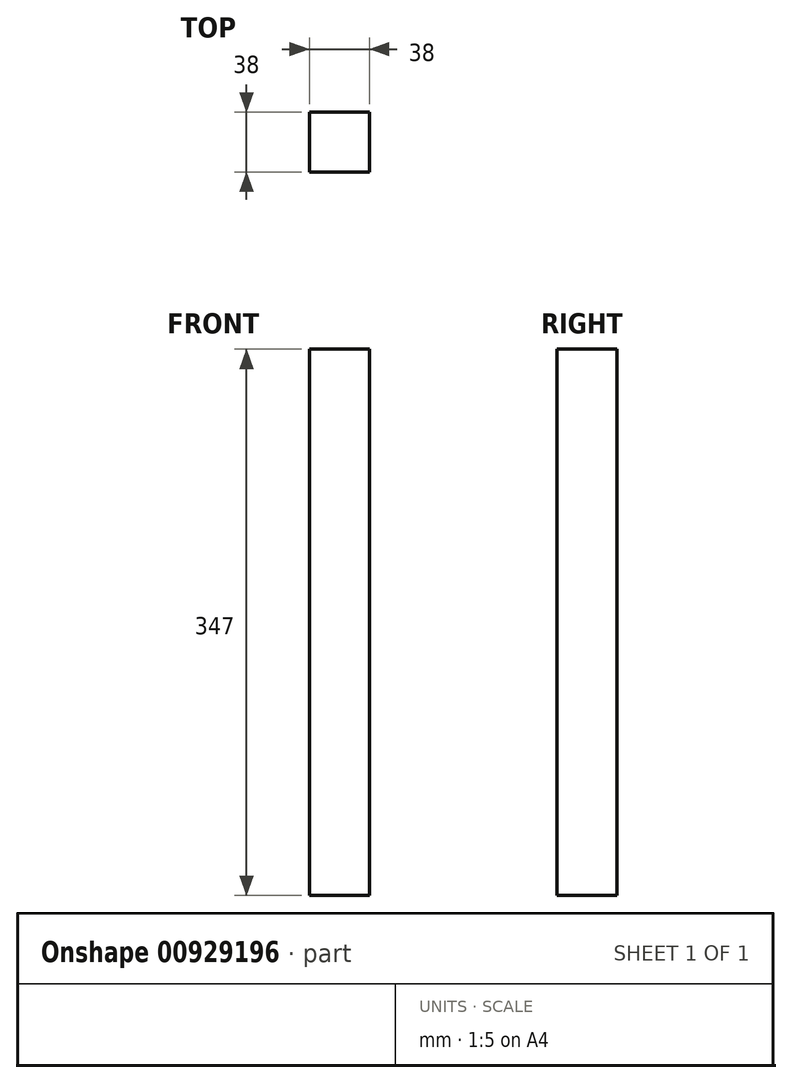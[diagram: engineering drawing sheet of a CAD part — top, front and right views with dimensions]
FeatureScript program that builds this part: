
annotation { "Feature Type Name" : "Feature", "Feature Type Description" : "" }
export const myFeature = defineFeature(function(context is Context, id is Id, definition is map)
    precondition{}
    {
        {
            var Q0;
            Q0=qCreatedBy(makeId("Front.planeOp"),FACE);
            var sketch = newSketch(context, id + "F0", { "sketchPlane" : qUnion([Q0])});
            skLineSegment(sketch, "E0.bottom", {"start": v(-24.87, 284.07) * mm, "end": v(13.13, 284.07) * mm});
            skLineSegment(sketch, "E0.top", {"start": v(-24.87, -62.93) * mm, "end": v(13.13, -62.93) * mm});
            skLineSegment(sketch, "E0.left", {"start": v(-24.87, 284.07) * mm, "end": v(-24.87, -62.93) * mm});
            skLineSegment(sketch, "E0.right", {"start": v(13.13, 284.07) * mm, "end": v(13.13, -62.93) * mm});
            skSolve(sketch);
        }
        {
            var Q0;
            Q0 = qSketchRegion(id + "F0", true);
            extrude(context, id + "F1", {"entities" : qUnion([Q0]), "depth" : 38 * mm, "offsetDistance" : 25 * mm});
        }
    });
